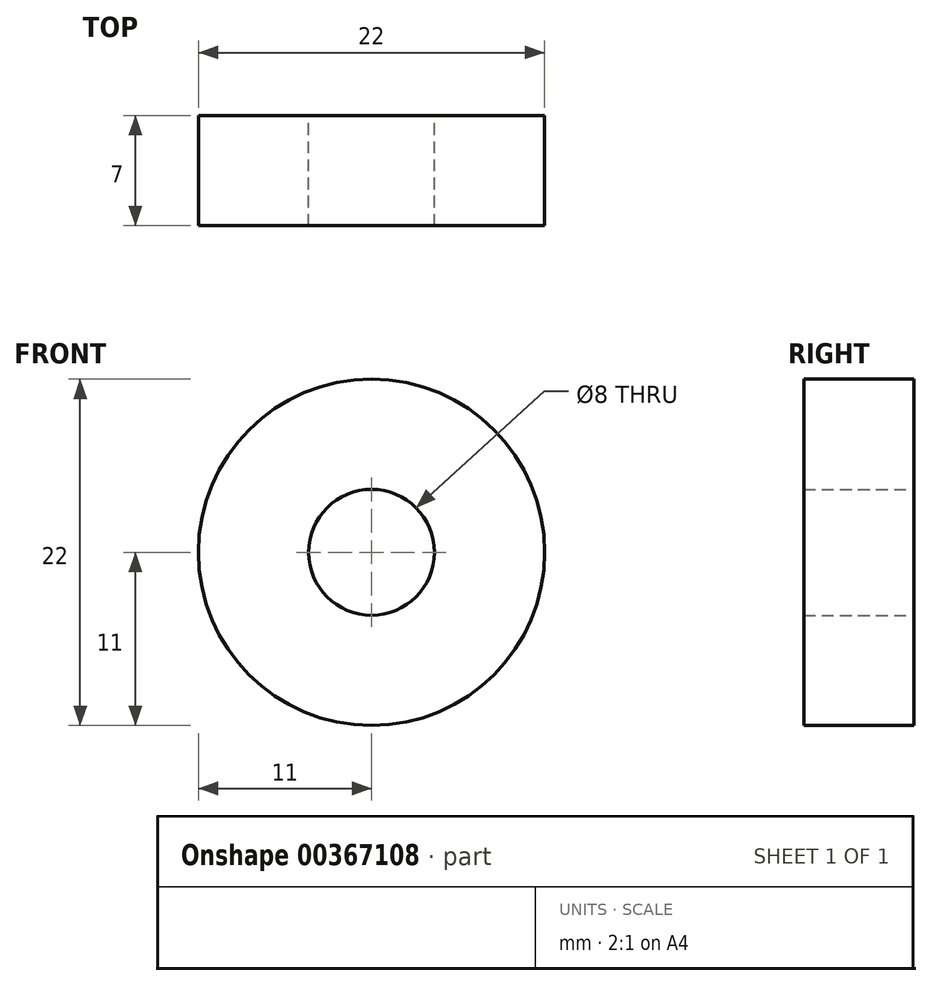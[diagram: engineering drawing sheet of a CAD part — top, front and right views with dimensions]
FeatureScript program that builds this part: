
annotation { "Feature Type Name" : "Feature", "Feature Type Description" : "" }
export const myFeature = defineFeature(function(context is Context, id is Id, definition is map)
    precondition{}
    {
        {
            var Q0;
            Q0=qCreatedBy(makeId("Front.planeOp"),FACE);
            var sketch = newSketch(context, id + "F0", { "sketchPlane" : qUnion([Q0])});
            skCircle(sketch, "E0", {"center": v(0, 0) * mm, "radius": 11 * mm});
            skCircle(sketch, "E1", {"center": v(0, 0) * mm, "radius": 4 * mm});
            skSolve(sketch);
        }
        {
            var Q0;
            Q0 = qSketchRegion(id + "F0", true);
            extrude(context, id + "F1", {"entities" : qUnion([Q0]), "endBound" : BoundingType.SYMMETRIC, "depth" : 7 * mm});
        }
    });
